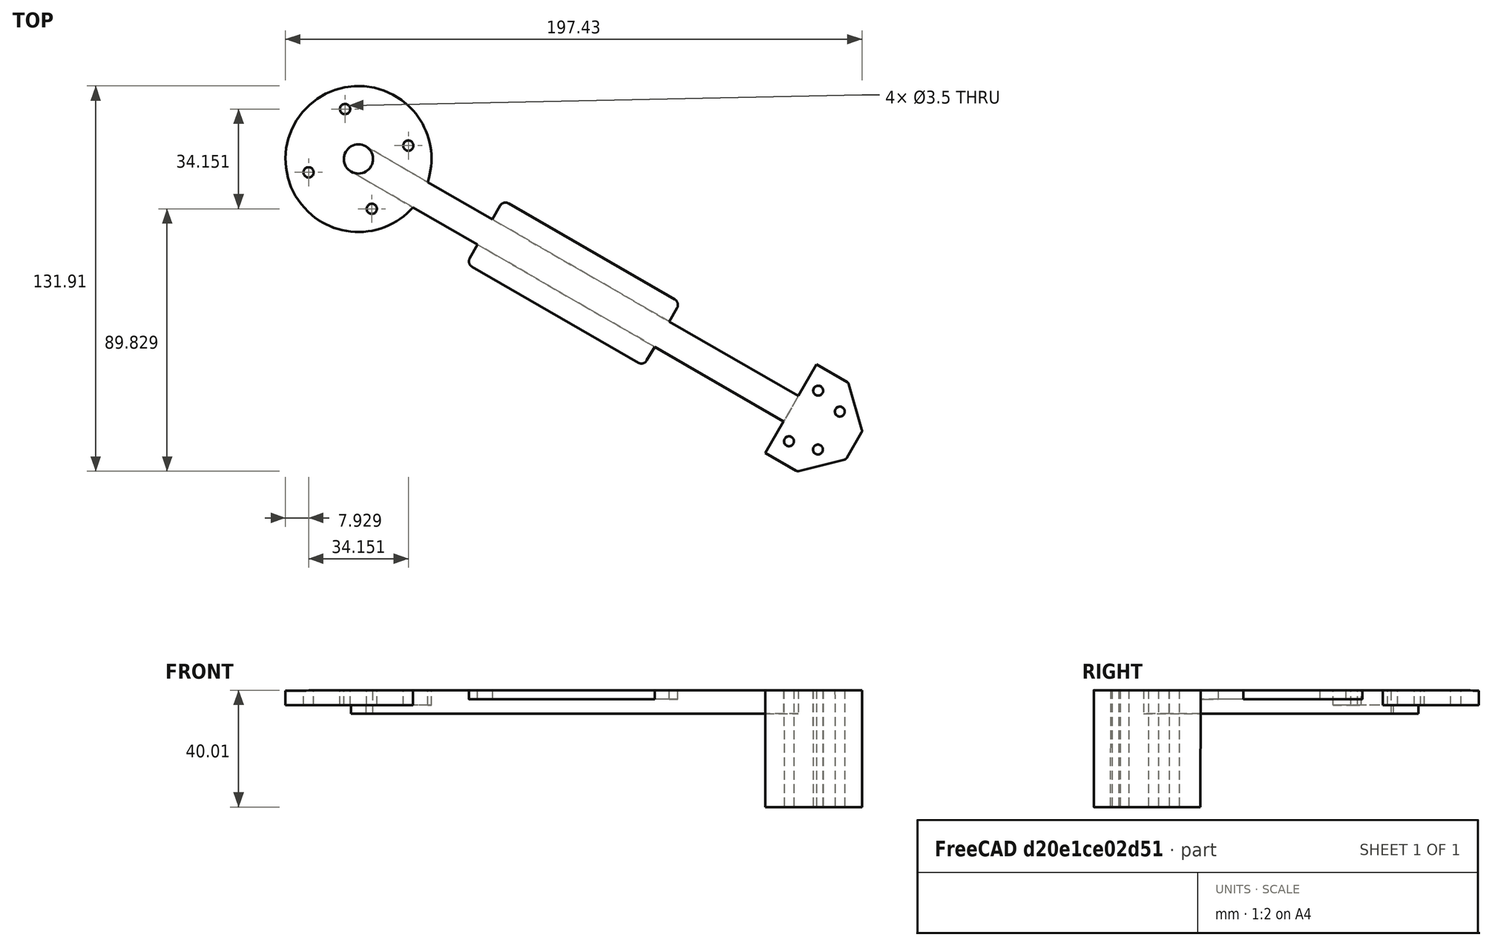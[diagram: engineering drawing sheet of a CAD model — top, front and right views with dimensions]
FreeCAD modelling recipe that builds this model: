
FCSTD DOCUMENT  (FreeCAD 1.0R39285 (Git))
Label: landing_gear
License: All rights reserved
LicenseURL: http://en.wikipedia.org/wiki/All_rights_reserved
objects: Sketcher::SketchObject×1, PartDesign::Body×1, Spreadsheet::Sheet×1, Part::FeaturePython×1
note: 4 computed .brp shape members not serialized (recipe doc carries the construction recipe); baked Part::Feature solids carry a one-line shape summary decoded from their .brp

FEATURE [Sketcher::SketchObject] Sketch001  label="mount_holes"
  ArcFitTolerance = 1e-06
  AttachmentSupport = -> [XY_Plane]
  FullyConstrained = true
  MakeInternals = false
  MapMode = 5
  expr: Constraints[6] = 22 mm
  sketch-geometry (8):
    g0: Circle CenterX=22 CenterY=34.5 CenterZ=0 NormalX=0 NormalY=0 NormalZ=1 AngleXU=0 Radius=1.75
    g1: Circle CenterX=38.7033 CenterY=23.5 CenterZ=0 NormalX=0 NormalY=0 NormalZ=1 AngleXU=0 Radius=1.75
    g2: Circle CenterX=29.3317 CenterY=41.3005 CenterZ=0 NormalX=0 NormalY=0 NormalZ=1 AngleXU=0 Radius=1.75
    g3: Circle CenterX=41.8258 CenterY=33 CenterZ=0 NormalX=0 NormalY=0 NormalZ=1 AngleXU=0 Radius=1.75
    g4: Circle CenterX=22 CenterY=167.5 CenterZ=0 NormalX=0 NormalY=0 NormalZ=1 AngleXU=0 Radius=1.75
    g5: Circle CenterX=31.5 CenterY=185.1 CenterZ=0 NormalX=0 NormalY=0 NormalZ=1 AngleXU=0 Radius=1.75
    g6: Circle CenterX=38.6414 CenterY=178.1 CenterZ=0 NormalX=0 NormalY=0 NormalZ=1 AngleXU=0 Radius=1.75
    g7: Circle CenterX=31.3341 CenterY=165 CenterZ=0 NormalX=0 NormalY=0 NormalZ=1 AngleXU=0 Radius=1.75
  constraints (24):
    c: Diameter(g1) = 3.5
    c: Equal(g1,g3)
    c: Equal(g3,g2)
    c: Equal(g2,g0)
    c: Distance(g0,g1) = 20
    c: DistanceY(g-1,g0) = 34.5
    c: DistanceX(g-1,g0) = 22
    c: Distance(g1,g3) = 10
    c: Distance(g0,g2) = 10
    c: Distance(g2,g3) = 15
    c: DistanceY(g-1,g1) = 23.5
    c: DistanceY(g-1,g3) = 33
    c: Equal(g2,g7)
    c: Equal(g7,g6)
    c: Equal(g6,g5)
    c: Equal(g5,g4)
    c: DistanceY(g0,g4) = 133
    c: Distance(g7,g6) = 15
    c: Distance(g4,g5) = 20
    c: Vertical(g4,g0)
    c: Distance(g6,g5) = 10
    c: DistanceX(g4,g5) = 9.5
    c: DistanceY(g6,g5) = 7
    c: DistanceY(g7,g4) = 2.5
FEATURE [PartDesign::Body] Body
  AllowCompound = false
  Group = -> [Sketch001]
  Origin = -> Origin
FEATURE [Spreadsheet::Sheet] Spreadsheet
  cells = A1='offset_x; B1(offset_x)=15; A2='offset_y; B2(offset_y)=15
FEATURE [Part::FeaturePython] b_leg_001_  label="leg_001"  # a2plus imported part (geometry in sourceFile) (typed FeaturePython)
  Placement = pos=(-135.318,347.802,-9.90955) rot=(-0.000143,0.000321,1;4.18879rad)
  a2p_Version = 0.4.68
  fixedPosition = true
  objectType = a2pPart
  sourceFile = ./leg.FCStd
  subassemblyImport = false
  timeLastImport = 1.7542e+09
  updateColors = true
